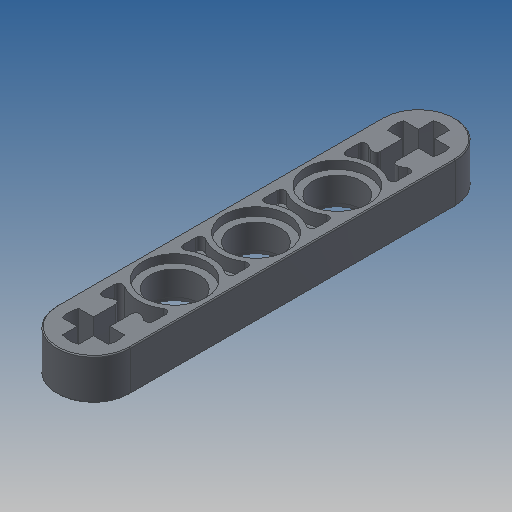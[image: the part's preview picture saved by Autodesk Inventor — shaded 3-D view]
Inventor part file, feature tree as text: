
AUTODESK INVENTOR PART (.ipt)
format: ipt  version: 2022.2 (Build 262287010, 287A)  size: 285,696 bytes
history: native  units: mm
features: extrude x3, sketch x2, mirror x1, fillet x1
ambient origin geometry x8: Origin, YZ Plane, XZ Plane, XY Plane, X Axis, Y Axis, Z Axis, Center Point
bodies: Solid1 (feature_tree)
feature tree (7):
  sketch  "Sketch1"  dims[d8=4.8mm d9=6.4mm]
  extrude  "Extrusion1"  Depth=6.4mm
  extrude  "Extrusion9"  Depth=7.2mm
  extrude  "Extrusion7"  Depth=8.0mm
  mirror  "Mirror1"
  fillet  "Fillet1"  Radius=0.8mm
  sketch  "Sketch6"  dims[d14=4.0mm d15=0.0mm d32=7.2mm d34=8.0mm d41=0.8mm d42=0.0mm d45=0.1mm d46=0.4mm d52=1.6mm d53=6.2mm d54=45.0deg d55=1.6mm d56=0.0mm]
